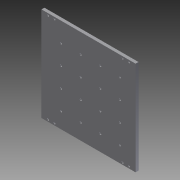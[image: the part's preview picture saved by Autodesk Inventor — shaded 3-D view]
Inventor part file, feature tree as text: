
AUTODESK INVENTOR PART (.ipt)
format: ipt  version: 2012 (Build 160160000, 160)  size: 111,104 bytes
history: native  units: in
note: dims shown in document units (in); Inventor stores cm internally (conversion verified against a paired STEP export)
features: hole x9, extrude x1, pattern_linear x1, sketch x1
ambient origin geometry x8: Origin, YZ Plane, XZ Plane, XY Plane, X Axis, Y Axis, Z Axis, Center Point
bodies: Solid1 (feature_tree)
feature tree (12):
  extrude  "Extrusion1"  Depth=12.0in
  hole  "Hole1"  [1 undecoded]
  hole  "Hole2"  [1 undecoded]
  hole  "Hole3"  [1 undecoded]
  hole  "Hole4"  [1 undecoded]
  hole  "Hole5"  [1 undecoded]
  hole  "Hole6"  [1 undecoded]
  hole  "Hole7"  [1 undecoded]
  hole  "Hole8"  [1 undecoded]
  hole  "Hole9"  [1 undecoded]
  pattern_linear  "Rectangular Pattern1"  Spacing1=2.5in  [1 undecoded]
  sketch  "Sketch1"  dims[d0=12.0in d1=12.0in d2=0.375in d3=0.0in d4=0.84in d5=0.25in d6=0.25in d7=0.75in d8=0.375in d9=0.25in d10=0.5635in d11=1.0in d12=0.8108in d13=1.66in d14=0.25in d15=0.25in d16=0.75in d17=0.375in d18=0.25in d19=0.5635in d20=1.0in d21=0.8108in d22=0.25in d23=1.66in d24=0.25in d25=0.75in d26=0.375in d27=0.25in d28=0.5635in d29=1.0in d30=0.8108in d31=0.25in d32=0.84in d33=0.25in d34=0.75in d35=0.375in d36=0.25in d37=0.5635in d38=1.0in d39=0.8108in d40=0.84in d41=0.25in d42=0.25in d43=0.75in d44=0.375in d45=0.25in d46=0.5635in d47=1.0in d48=0.8108in d49=0.25in d50=1.66in d51=0.25in d52=0.75in d53=0.375in d54=0.25in d55=0.5635in d56=1.0in d57=0.8108in d58=1.66in d59=0.25in d60=0.25in d61=0.75in d62=0.375in d63=0.25in d64=0.5635in d65=1.0in d66=0.8108in d67=0.25in d68=0.84in d69=0.25in d70=0.75in d71=0.375in d72=0.25in d73=0.5635in d74=1.0in d75=0.8108in d76=2.5in d77=2.5in d78=0.25in d79=0.75in d80=0.375in d81=0.25in d82=0.5635in d83=1.0in d84=0.8108in d85=1.5748in d87=2.5in d88=1.5748in d90=2.5in]
note: 10 required parameter values undecoded (feature->parameter linkage not recoverable at this tier; creation-order binding heuristic only, values carry confidence <= 0.55)
